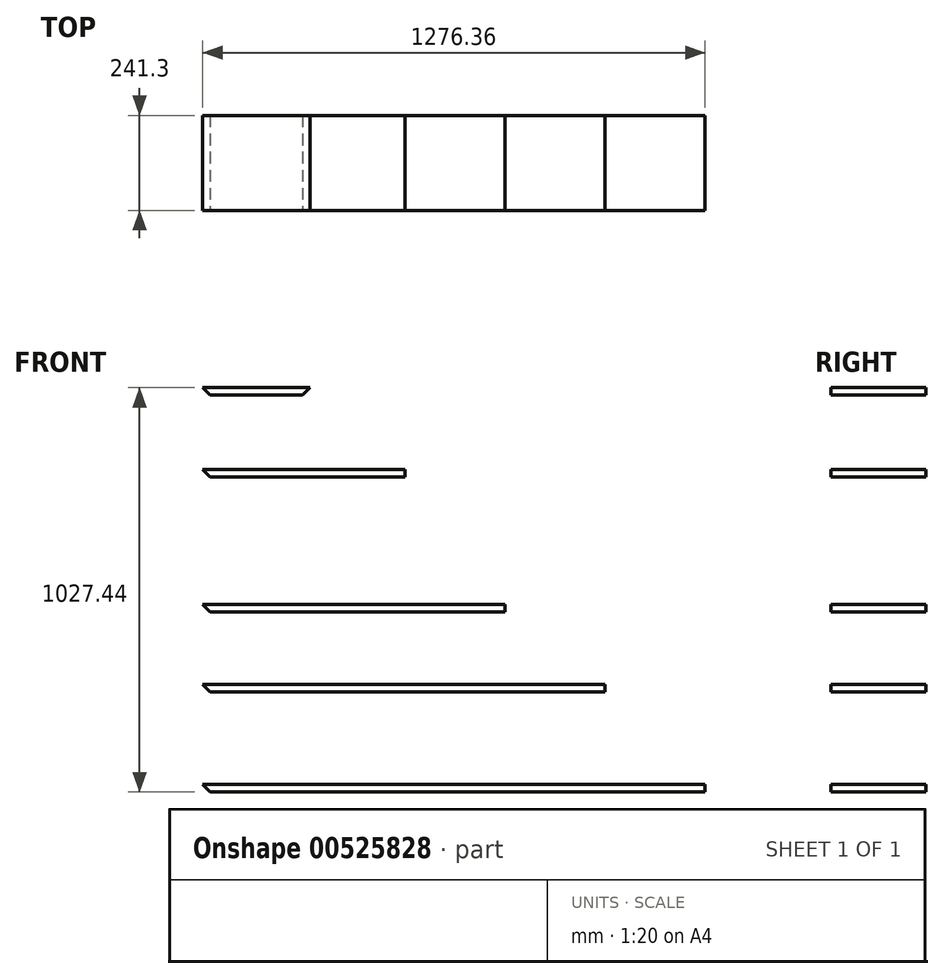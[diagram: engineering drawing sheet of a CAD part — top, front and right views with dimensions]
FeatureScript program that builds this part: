
annotation { "Feature Type Name" : "Feature", "Feature Type Description" : "" }
export const myFeature = defineFeature(function(context is Context, id is Id, definition is map)
    precondition{}
    {
        {
            var Q0;
            Q0=qCreatedBy(makeId("Front.planeOp"),FACE);
            var sketch = newSketch(context, id + "F0", { "sketchPlane" : qUnion([Q0])});
            skLineSegment(sketch, "E0.bottom", {"start": v(638.18, 9.52) * mm, "end": v(-638.18, 9.52) * mm});
            skLineSegment(sketch, "E0.top", {"start": v(638.18, -9.53) * mm, "end": v(-638.18, -9.53) * mm});
            skLineSegment(sketch, "E0.left", {"start": v(638.18, 9.52) * mm, "end": v(638.18, -9.53) * mm});
            skLineSegment(sketch, "E0.right", {"start": v(-638.18, 9.52) * mm, "end": v(-638.18, -9.53) * mm});
            skPoint(sketch, "E0.middle", {"position": v(0, 0) * mm});
            skSolve(sketch);
        }
        {
            var Q0;
            Q0=qSketchRegion(id+"F0",true);
            extrude(context, id + "F1", {"entities" : qUnion([Q0]), "depth" : 241.3 * mm});
        }
        {
            var Q0;
            Q0=makeQuery(id+"F1.opExtrude","CAP_FACE",FACE,{"disambiguationData":[OSD([sQuery(id+"F0.wireOp",EDGE,"E0.bottom"),sQuery(id+"F0.wireOp",EDGE,"E0.top"),sQuery(id+"F0.wireOp",EDGE,"E0.left"),sQuery(id+"F0.wireOp",EDGE,"E0.right")])],"isStart":false});
            var sketch = newSketch(context, id + "F2", { "sketchPlane" : qUnion([Q0])});
            skLineSegment(sketch, "E1", {"start": v(-638.18, 9.52) * mm, "end": v(-638.18, -9.53) * mm});
            skLineSegment(sketch, "E2", {"start": v(-638.18, -9.53) * mm, "end": v(-619.12, -9.53) * mm});
            skLineSegment(sketch, "E3", {"start": v(-619.12, -9.53) * mm, "end": v(-638.18, 9.52) * mm});
            skSolve(sketch);
        }
        {
            var Q0;
            Q0=qSketchRegion(id+"F2",true);
            extrude(context, id + "F3", {"entities" : qUnion([Q0]), "operationType" : NewBodyOperationType.REMOVE, "endBound" : BoundingType.THROUGH_ALL, "oppositeDirection" : true, "depth" : 25.4 * mm});
        }
        {
            var Q0;
            Q0=makeQuery(id+"F1.opExtrude","SWEPT_BODY",BODY,{"disambiguationData":[OSD([sQuery(id+"F0.wireOp",EDGE,"E0.bottom"),sQuery(id+"F0.wireOp",EDGE,"E0.top"),sQuery(id+"F0.wireOp",EDGE,"E0.left"),sQuery(id+"F0.wireOp",EDGE,"E0.right")])]});
            transform(context, id + "F4", {"entities" : qUnion([Q0]), "transformType" : TransformType.TRANSLATION_3D, "dx" : 0 * mm, "dy" : 0 * mm, "dz" : 254 * mm, "makeCopy" : true});
        }
        {
            var Q0;
            Q0=makeQuery(id+"F4.opPattern","COPY",FACE,{"derivedFrom":makeQuery(id+"F1.opExtrude","CAP_FACE",FACE,{"disambiguationData":[OSD([sQuery(id+"F0.wireOp",EDGE,"E0.bottom"),sQuery(id+"F0.wireOp",EDGE,"E0.top"),sQuery(id+"F0.wireOp",EDGE,"E0.left"),sQuery(id+"F0.wireOp",EDGE,"E0.right")])],"isStart":false}),"instanceName":"1"});
            var sketch = newSketch(context, id + "F5", { "sketchPlane" : qUnion([Q0])});
            skLineSegment(sketch, "E4.bottom", {"start": v(638.18, 263.52) * mm, "end": v(384.18, 263.52) * mm});
            skLineSegment(sketch, "E4.top", {"start": v(638.18, 244.47) * mm, "end": v(384.18, 244.47) * mm});
            skLineSegment(sketch, "E4.left", {"start": v(638.18, 263.52) * mm, "end": v(638.18, 244.47) * mm});
            skLineSegment(sketch, "E4.right", {"start": v(384.18, 263.52) * mm, "end": v(384.18, 244.47) * mm});
            skSolve(sketch);
        }
        {
            var Q0;
            Q0=qSketchRegion(id+"F5",true);
            extrude(context, id + "F6", {"entities" : qUnion([Q0]), "operationType" : NewBodyOperationType.REMOVE, "endBound" : BoundingType.THROUGH_ALL, "oppositeDirection" : true, "depth" : 25.4 * mm});
        }
        {
            var Q0;
            Q0=makeQuery(id+"F4.opPattern","COPY",BODY,{"derivedFrom":makeQuery(id+"F1.opExtrude","SWEPT_BODY",BODY,{"disambiguationData":[OSD([sQuery(id+"F0.wireOp",EDGE,"E0.bottom"),sQuery(id+"F0.wireOp",EDGE,"E0.top"),sQuery(id+"F0.wireOp",EDGE,"E0.left"),sQuery(id+"F0.wireOp",EDGE,"E0.right")])]}),"instanceName":"1"});
            transform(context, id + "F7", {"entities" : qUnion([Q0]), "transformType" : TransformType.TRANSLATION_3D, "dx" : 0 * mm, "dy" : 0 * mm, "dz" : 203.2 * mm, "makeCopy" : true});
        }
        {
            var Q0;
            Q0=makeQuery(id+"F7.opPattern","COPY",FACE,{"derivedFrom":makeQuery(id+"F4.opPattern","COPY",FACE,{"derivedFrom":makeQuery(id+"F1.opExtrude","CAP_FACE",FACE,{"disambiguationData":[OSD([sQuery(id+"F0.wireOp",EDGE,"E0.bottom"),sQuery(id+"F0.wireOp",EDGE,"E0.top"),sQuery(id+"F0.wireOp",EDGE,"E0.left"),sQuery(id+"F0.wireOp",EDGE,"E0.right")])],"isStart":false}),"instanceName":"1"}),"instanceName":"1"});
            var sketch = newSketch(context, id + "F8", { "sketchPlane" : qUnion([Q0])});
            skLineSegment(sketch, "E5.bottom", {"start": v(384.18, 466.72) * mm, "end": v(130.18, 466.72) * mm});
            skLineSegment(sketch, "E5.top", {"start": v(384.18, 447.67) * mm, "end": v(130.18, 447.67) * mm});
            skLineSegment(sketch, "E5.left", {"start": v(384.18, 466.72) * mm, "end": v(384.18, 447.67) * mm});
            skLineSegment(sketch, "E5.right", {"start": v(130.18, 466.72) * mm, "end": v(130.18, 447.67) * mm});
            skSolve(sketch);
        }
        {
            var Q0;
            Q0=qSketchRegion(id+"F8",true);
            extrude(context, id + "F9", {"entities" : qUnion([Q0]), "operationType" : NewBodyOperationType.REMOVE, "endBound" : BoundingType.THROUGH_ALL, "oppositeDirection" : true, "depth" : 25.4 * mm});
        }
        {
            var Q0;
            Q0=makeQuery(id+"F7.opPattern","COPY",BODY,{"derivedFrom":makeQuery(id+"F4.opPattern","COPY",BODY,{"derivedFrom":makeQuery(id+"F1.opExtrude","SWEPT_BODY",BODY,{"disambiguationData":[OSD([sQuery(id+"F0.wireOp",EDGE,"E0.bottom"),sQuery(id+"F0.wireOp",EDGE,"E0.top"),sQuery(id+"F0.wireOp",EDGE,"E0.left"),sQuery(id+"F0.wireOp",EDGE,"E0.right")])]}),"instanceName":"1"}),"instanceName":"1"});
            transform(context, id + "F10", {"entities" : qUnion([Q0]), "transformType" : TransformType.TRANSLATION_3D, "dx" : 0 * mm, "dy" : 0 * mm, "dz" : 342.9 * mm, "makeCopy" : true});
        }
        {
            var Q0;
            Q0=makeQuery(id+"F10.opPattern","COPY",FACE,{"derivedFrom":makeQuery(id+"F7.opPattern","COPY",FACE,{"derivedFrom":makeQuery(id+"F4.opPattern","COPY",FACE,{"derivedFrom":makeQuery(id+"F1.opExtrude","CAP_FACE",FACE,{"disambiguationData":[OSD([sQuery(id+"F0.wireOp",EDGE,"E0.bottom"),sQuery(id+"F0.wireOp",EDGE,"E0.top"),sQuery(id+"F0.wireOp",EDGE,"E0.left"),sQuery(id+"F0.wireOp",EDGE,"E0.right")])],"isStart":false}),"instanceName":"1"}),"instanceName":"1"}),"instanceName":"1"});
            var sketch = newSketch(context, id + "F11", { "sketchPlane" : qUnion([Q0])});
            skLineSegment(sketch, "E6.bottom", {"start": v(130.18, 809.62) * mm, "end": v(-123.82, 809.62) * mm});
            skLineSegment(sketch, "E6.top", {"start": v(130.18, 790.57) * mm, "end": v(-123.82, 790.57) * mm});
            skLineSegment(sketch, "E6.left", {"start": v(130.18, 809.62) * mm, "end": v(130.18, 790.57) * mm});
            skLineSegment(sketch, "E6.right", {"start": v(-123.82, 809.62) * mm, "end": v(-123.82, 790.57) * mm});
            skSolve(sketch);
        }
        {
            var Q0;
            Q0=qSketchRegion(id+"F11",true);
            extrude(context, id + "F12", {"entities" : qUnion([Q0]), "operationType" : NewBodyOperationType.REMOVE, "endBound" : BoundingType.THROUGH_ALL, "oppositeDirection" : true, "depth" : 25.4 * mm});
        }
        {
            var Q0;
            Q0=makeQuery(id+"F10.opPattern","COPY",BODY,{"derivedFrom":makeQuery(id+"F7.opPattern","COPY",BODY,{"derivedFrom":makeQuery(id+"F4.opPattern","COPY",BODY,{"derivedFrom":makeQuery(id+"F1.opExtrude","SWEPT_BODY",BODY,{"disambiguationData":[OSD([sQuery(id+"F0.wireOp",EDGE,"E0.bottom"),sQuery(id+"F0.wireOp",EDGE,"E0.top"),sQuery(id+"F0.wireOp",EDGE,"E0.left"),sQuery(id+"F0.wireOp",EDGE,"E0.right")])]}),"instanceName":"1"}),"instanceName":"1"}),"instanceName":"1"});
            transform(context, id + "F13", {"entities" : qUnion([Q0]), "transformType" : TransformType.TRANSLATION_3D, "dx" : 0 * mm, "dy" : 0 * mm, "dz" : 208.28 * mm, "makeCopy" : true});
        }
        {
            var Q0;
            Q0=makeQuery(id+"F13.opPattern","COPY",FACE,{"derivedFrom":makeQuery(id+"F10.opPattern","COPY",FACE,{"derivedFrom":makeQuery(id+"F7.opPattern","COPY",FACE,{"derivedFrom":makeQuery(id+"F4.opPattern","COPY",FACE,{"derivedFrom":makeQuery(id+"F1.opExtrude","CAP_FACE",FACE,{"disambiguationData":[OSD([sQuery(id+"F0.wireOp",EDGE,"E0.bottom"),sQuery(id+"F0.wireOp",EDGE,"E0.top"),sQuery(id+"F0.wireOp",EDGE,"E0.left"),sQuery(id+"F0.wireOp",EDGE,"E0.right")])],"isStart":false}),"instanceName":"1"}),"instanceName":"1"}),"instanceName":"1"}),"instanceName":"1"});
            var sketch = newSketch(context, id + "F14", { "sketchPlane" : qUnion([Q0])});
            skLineSegment(sketch, "E7", {"start": v(-384.17, 998.85) * mm, "end": v(-365.12, 1017.9) * mm});
            skLineSegment(sketch, "E8", {"start": v(-365.12, 1017.9) * mm, "end": v(-123.82, 1017.9) * mm});
            skLineSegment(sketch, "E9", {"start": v(-123.82, 1017.9) * mm, "end": v(-123.82, 998.85) * mm});
            skLineSegment(sketch, "E10", {"start": v(-123.82, 998.85) * mm, "end": v(-384.18, 998.85) * mm});
            skSolve(sketch);
        }
        {
            var Q0;
            Q0=qSketchRegion(id+"F14",true);
            extrude(context, id + "F15", {"entities" : qUnion([Q0]), "operationType" : NewBodyOperationType.REMOVE, "endBound" : BoundingType.THROUGH_ALL, "oppositeDirection" : true, "depth" : 25.4 * mm});
        }
    });
